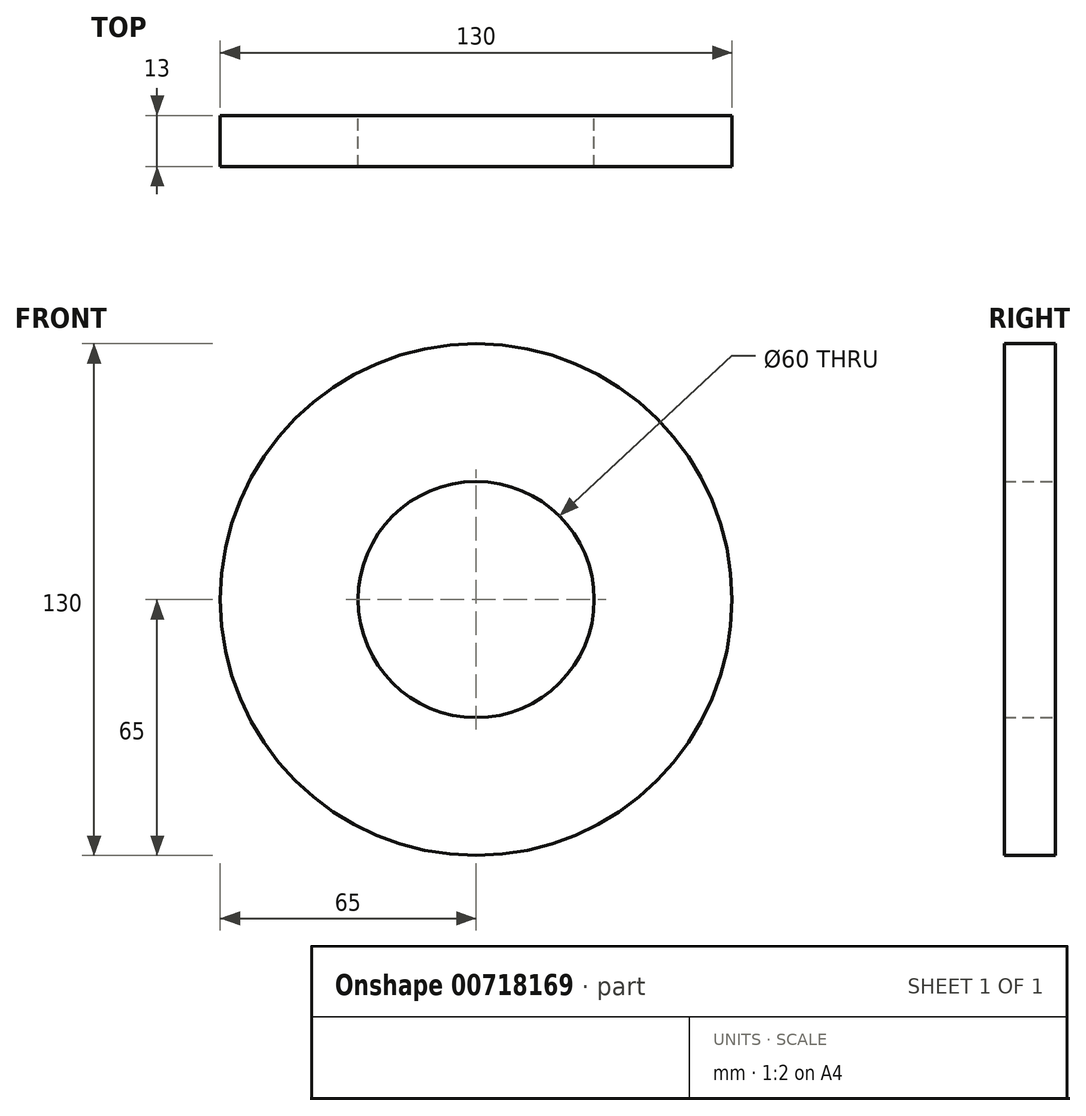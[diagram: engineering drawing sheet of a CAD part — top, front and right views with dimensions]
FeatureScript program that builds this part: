
annotation { "Feature Type Name" : "Feature", "Feature Type Description" : "" }
export const myFeature = defineFeature(function(context is Context, id is Id, definition is map)
    precondition{}
    {
        {
            var Q0;
            Q0=qCreatedBy(makeId("Front.planeOp"),FACE);
            var sketch = newSketch(context, id + "F0", { "sketchPlane" : qUnion([Q0])});
            skCircle(sketch, "E0", {"center": v(0, 0) * mm, "radius": 65 * mm});
            skCircle(sketch, "E1", {"center": v(0, 0) * mm, "radius": 30 * mm});
            skSolve(sketch);
        }
        {
            var Q0;
            Q0=makeQuery(id+"F0.imprint","IMPRINT",FACE,{"disambiguationData":[TD([[makeQuery(id+"F0.imprint","IMPRINT",EDGE,{"derivedFrom":sQuery(id+"F0.wireOp",EDGE,"E0")}),1.0]])]});
            extrude(context, id + "F1", {"entities" : qUnion([Q0]), "depth" : 13 * mm, "offsetDistance" : 25 * mm});
        }
    });
